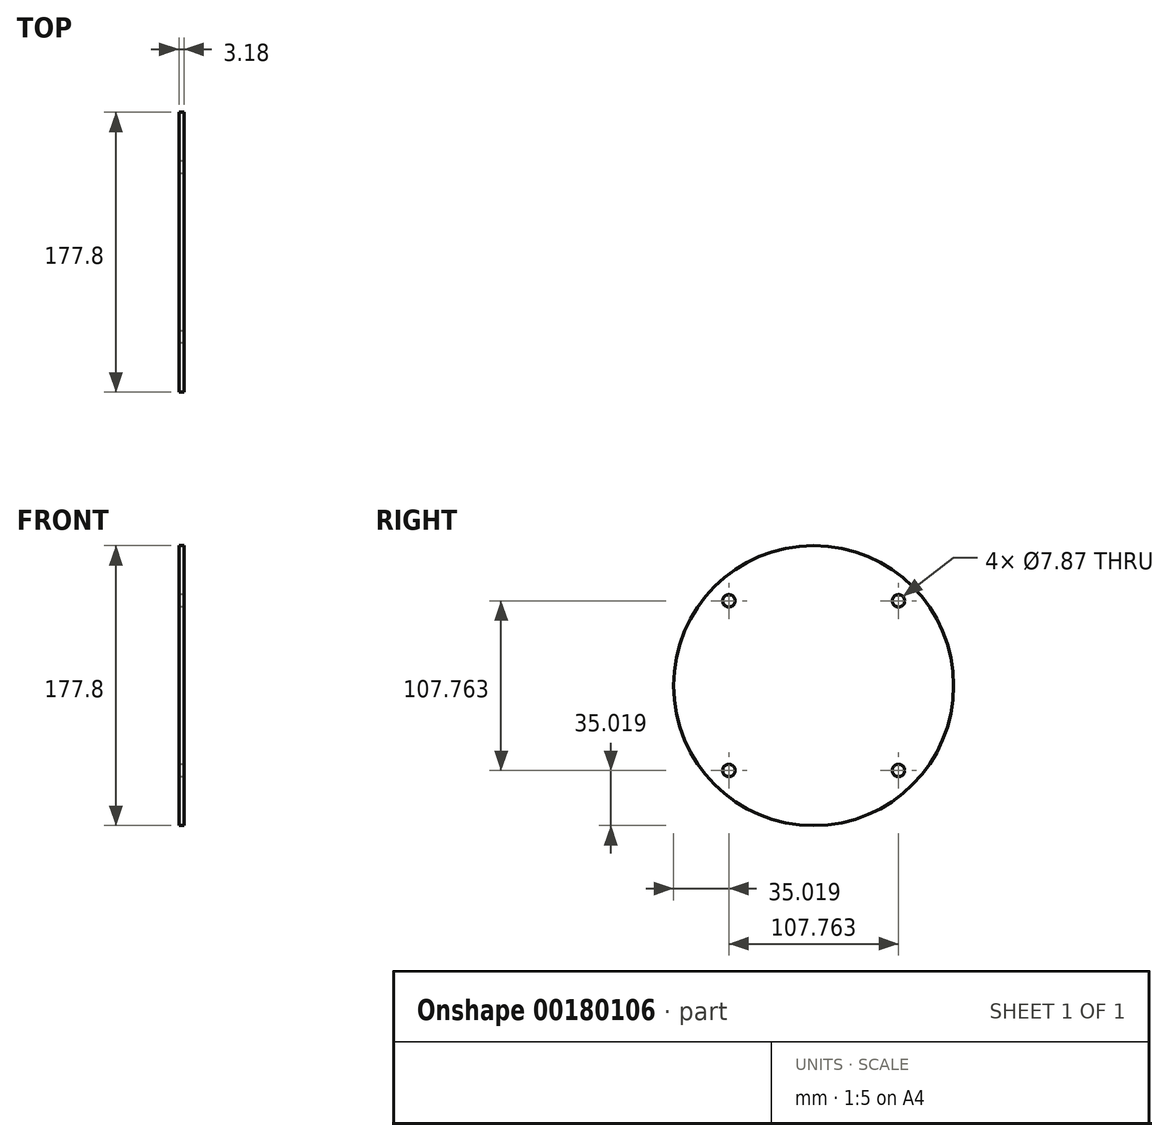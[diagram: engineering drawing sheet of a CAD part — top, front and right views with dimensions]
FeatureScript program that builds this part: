
annotation { "Feature Type Name" : "Feature", "Feature Type Description" : "" }
export const myFeature = defineFeature(function(context is Context, id is Id, definition is map)
    precondition{}
    {
        {
            var Q0;
            Q0=qCreatedBy(makeId("Right.planeOp"),FACE);
            var sketch = newSketch(context, id + "F0", { "sketchPlane" : qUnion([Q0])});
            skCircle(sketch, "E0", {"center": v(0, 0) * mm, "radius": 88.9 * mm});
            skCircle(sketch, "E1", {"center": v(0, 0) * mm, "radius": 76.2 * mm, "construction": true});
            skLineSegment(sketch, "E2", {"start": v(0, 0) * mm, "end": v(0, 114.77) * mm, "construction": true});
            skLineSegment(sketch, "E3", {"start": v(0, 0) * mm, "end": v(-92.26, 92.26) * mm, "construction": true});
            skCircle(sketch, "E4", {"center": v(-53.88, 53.88) * mm, "radius": 3.94 * mm});
            skCircle(sketch, "E5.1.0", {"center": v(-53.88, -53.88) * mm, "radius": 3.94 * mm});
            skCircle(sketch, "E5.2.0", {"center": v(53.88, -53.88) * mm, "radius": 3.94 * mm});
            skCircle(sketch, "E5.3.0", {"center": v(53.88, 53.88) * mm, "radius": 3.94 * mm});
            skSolve(sketch);
        }
        {
            var Q0;
            Q0=qSketchRegion(id+"F0",true);
            extrude(context, id + "F1", {"entities" : qUnion([Q0]), "depth" : 3.17 * mm});
        }
    });
